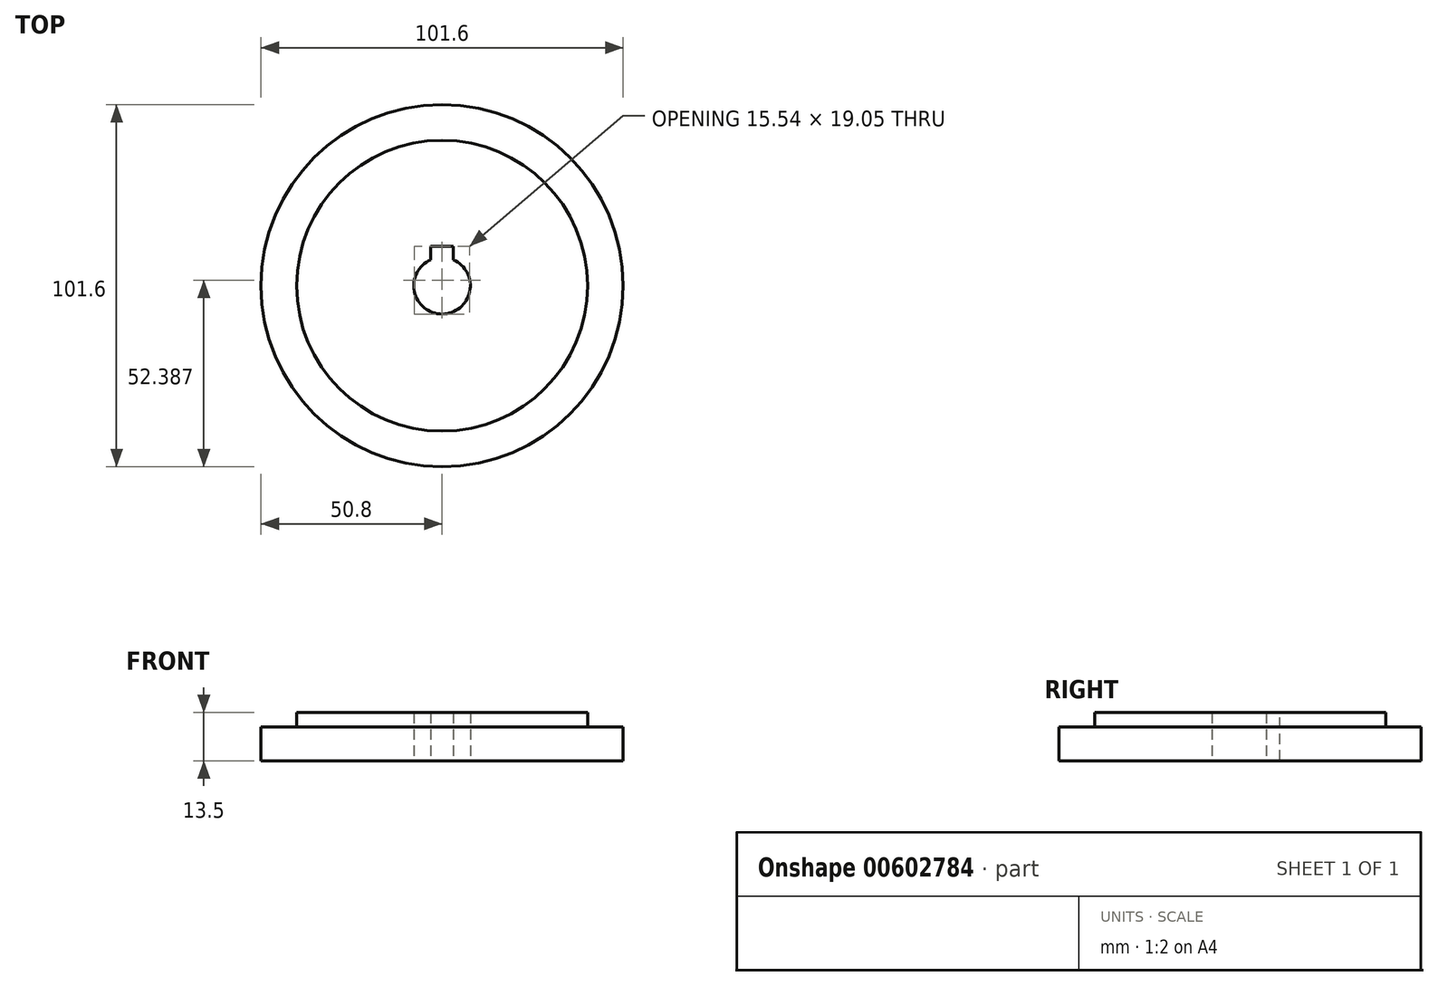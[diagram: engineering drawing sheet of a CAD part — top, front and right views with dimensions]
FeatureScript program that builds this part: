
annotation { "Feature Type Name" : "Feature", "Feature Type Description" : "" }
export const myFeature = defineFeature(function(context is Context, id is Id, definition is map)
    precondition{}
    {
        {
            var Q0;
            Q0=qCreatedBy(makeId("Top.planeOp"),FACE);
            var sketch = newSketch(context, id + "F0", { "sketchPlane" : qUnion([Q0])});
            skCircle(sketch, "E0", {"center": v(0, 0) * mm, "radius": 50.8 * mm});
            skCircle(sketch, "E1", {"center": v(0, 0) * mm, "radius": 7.94 * mm});
            skSolve(sketch);
        }
        {
            var Q0;
            Q0=makeQuery(id+"F0.imprint","IMPRINT",FACE,{"disambiguationData":[TD([[makeQuery(id+"F0.imprint","IMPRINT",EDGE,{"derivedFrom":sQuery(id+"F0.wireOp",EDGE,"E0")}),1.0]])]});
            extrude(context, id + "F1", {"entities" : qUnion([Q0]), "depth" : 4.5 * mm, "offsetDistance" : 25.4 * mm, "hasSecondDirection" : true, "secondDirectionOppositeDirection" : true, "secondDirectionDepth" : 5 * mm});
        }
        {
            var Q0;
            Q0=makeQuery(id+"F1.opExtrude","CAP_FACE",FACE,{"disambiguationData":[OSD([sQuery(id+"F0.wireOp",EDGE,"E0"),sQuery(id+"F0.wireOp",EDGE,"E1")])],"isStart":false});
            var sketch = newSketch(context, id + "F2", { "sketchPlane" : qUnion([Q0])});
            skCircle(sketch, "E2.0", {"center": v(0, 0) * mm, "radius": 40.8 * mm});
            skSolve(sketch);
        }
        {
            var Q0;
            Q0=makeQuery(id+"F2.imprint","IMPRINT",FACE,{"disambiguationData":[TD([[makeQuery(id+"F2.imprint","IMPRINT",EDGE,{"derivedFrom":sQuery(id+"F2.wireOp",EDGE,"E2.0")}),1.0]])]});
            extrude(context, id + "F3", {"entities" : qUnion([Q0]), "operationType" : NewBodyOperationType.ADD, "depth" : 4 * mm, "offsetDistance" : 25.4 * mm});
        }
        {
            var Q0;
            Q0=makeQuery(id+"F3.opExtrude","CAP_FACE",FACE,{"disambiguationData":[OSD([sQuery(id+"F0.wireOp",EDGE,"E1"),sQuery(id+"F2.wireOp",EDGE,"E2.0")])],"isStart":false});
            var sketch = newSketch(context, id + "F4", { "sketchPlane" : qUnion([Q0])});
            skLineSegment(sketch, "E3.bottom", {"start": v(3.18, 4.76) * mm, "end": v(-3.17, 4.76) * mm});
            skLineSegment(sketch, "E3.top", {"start": v(3.18, 11.11) * mm, "end": v(-3.17, 11.11) * mm});
            skLineSegment(sketch, "E3.left", {"start": v(3.18, 4.76) * mm, "end": v(3.18, 11.11) * mm});
            skLineSegment(sketch, "E3.right", {"start": v(-3.17, 4.76) * mm, "end": v(-3.17, 11.11) * mm});
            skPoint(sketch, "E3.middle", {"position": v(0, 7.94) * mm});
            skSolve(sketch);
        }
        {
            var Q0;
            Q0 = qSketchRegion(id + "F4", true);
            extrude(context, id + "F5", {"entities" : qUnion([Q0]), "operationType" : NewBodyOperationType.REMOVE, "endBound" : BoundingType.THROUGH_ALL, "oppositeDirection" : true, "depth" : 25.4 * mm, "offsetDistance" : 25.4 * mm});
        }
    });
